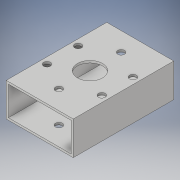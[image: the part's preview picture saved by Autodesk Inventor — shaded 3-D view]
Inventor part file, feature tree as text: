
AUTODESK INVENTOR PART (.ipt)
format: ipt  version: 2018 (Build 220112000, 112)  size: 147,968 bytes
history: native  units: in
note: dims shown in document units (in); Inventor stores cm internally (conversion verified against a paired STEP export)
features: extrude x3, sketch x3
ambient origin geometry x8: Origin, YZ Plane, XZ Plane, XY Plane, X Axis, Y Axis, Z Axis, Center Point
bodies: Solid1 (feature_tree)
feature tree (6):
  extrude  "Extrusion1"  Depth=1.0in
  extrude  "Extrusion2"  Depth=0.065in
  extrude  "Extrusion4"  Depth=0.065in
  sketch  "Sketch1"  dims[d0=0.065in d1=1.0in]
  sketch  "Sketch2"  dims[d2=2.0in d3=0.065in]
  sketch  "Sketch4"  dims[d4=0.065in d5=0.065in d6=3.0in d7=0.0in d8=0.75in d9=1.0in d10=1.5in d11=3.0in d12=0.0in d31=0.9375in d32=0.2031in d33=2.3622in d35=360.0deg d37=3.0in d38=0.0in]
